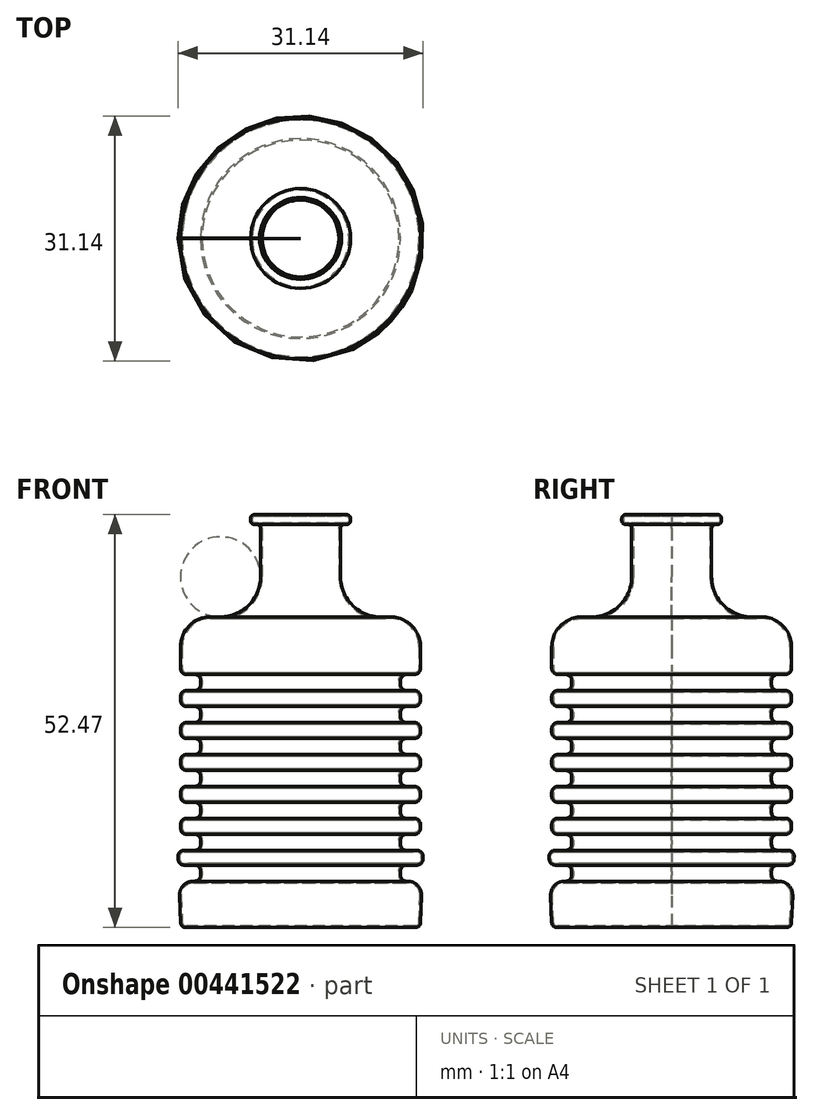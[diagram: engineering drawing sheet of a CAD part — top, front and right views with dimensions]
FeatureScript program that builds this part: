
annotation { "Feature Type Name" : "Feature", "Feature Type Description" : "" }
export const myFeature = defineFeature(function(context is Context, id is Id, definition is map)
    precondition{}
    {
        {
            var Q0;
            Q0=qCreatedBy(makeId("Front.planeOp"),FACE);
            var sketch = newSketch(context, id + "F0", { "sketchPlane" : qUnion([Q0])});
            skLineSegment(sketch, "E0", {"start": v(-5.2, 50.53) * mm, "end": v(-5.84, 50.53) * mm});
            skLineSegment(sketch, "E1", {"start": v(-6.35, 50.02) * mm, "end": v(-6.35, 49.77) * mm});
            skLineSegment(sketch, "E2", {"start": v(-5.84, 49.26) * mm, "end": v(-5.59, 49.26) * mm});
            skLineSegment(sketch, "E3", {"start": v(-5.08, 48.75) * mm, "end": v(-5.08, 46.72) * mm});
            skLineSegment(sketch, "E4", {"start": v(-5.08, 36.56) * mm, "end": v(-5.08, 36.56) * mm});
            skLineSegment(sketch, "E5", {"start": v(-15.24, 36.56) * mm, "end": v(-15.24, 36.56) * mm});
            skLineSegment(sketch, "E6", {"start": v(-14.6, -1.94) * mm, "end": v(-2.67, -1.94) * mm});
            skLineSegment(sketch, "E7", {"start": v(-15.24, 32.35) * mm, "end": v(-15.24, 30.97) * mm});
            skLineSegment(sketch, "E8", {"start": v(-14.48, 30.21) * mm, "end": v(-13.46, 30.21) * mm});
            skLineSegment(sketch, "E9", {"start": v(-12.7, 29.45) * mm, "end": v(-12.7, 28.94) * mm});
            skLineSegment(sketch, "E10", {"start": v(-13.46, 28.18) * mm, "end": v(-14.48, 28.18) * mm});
            skLineSegment(sketch, "E11", {"start": v(-15.24, 27.42) * mm, "end": v(-15.24, 26.9) * mm});
            skLineSegment(sketch, "E12", {"start": v(-14.48, 26.15) * mm, "end": v(-13.46, 26.15) * mm});
            skLineSegment(sketch, "E13", {"start": v(-12.7, 25.39) * mm, "end": v(-12.7, 24.88) * mm});
            skLineSegment(sketch, "E14", {"start": v(-13.46, 24.12) * mm, "end": v(-14.48, 24.12) * mm});
            skLineSegment(sketch, "E15", {"start": v(-15.24, 23.35) * mm, "end": v(-15.24, 22.85) * mm});
            skLineSegment(sketch, "E16", {"start": v(-14.48, 22.08) * mm, "end": v(-13.46, 22.08) * mm});
            skLineSegment(sketch, "E17", {"start": v(-12.7, 21.32) * mm, "end": v(-12.7, 20.81) * mm});
            skLineSegment(sketch, "E18", {"start": v(-13.46, 20.05) * mm, "end": v(-14.48, 20.05) * mm});
            skLineSegment(sketch, "E19", {"start": v(-15.24, 19.29) * mm, "end": v(-15.24, 18.8) * mm});
            skLineSegment(sketch, "E20", {"start": v(-14.48, 18.03) * mm, "end": v(-13.46, 18.03) * mm});
            skLineSegment(sketch, "E21", {"start": v(-12.7, 17.27) * mm, "end": v(-12.7, 16.76) * mm});
            skLineSegment(sketch, "E22", {"start": v(-13.46, 16) * mm, "end": v(-14.48, 16) * mm});
            skLineSegment(sketch, "E23", {"start": v(-15.24, 15.24) * mm, "end": v(-15.24, 14.73) * mm});
            skLineSegment(sketch, "E24", {"start": v(-14.48, 13.97) * mm, "end": v(-13.46, 13.97) * mm});
            skLineSegment(sketch, "E25", {"start": v(-12.7, 13.2) * mm, "end": v(-12.7, 12.7) * mm});
            skLineSegment(sketch, "E26", {"start": v(-13.46, 11.94) * mm, "end": v(-14.48, 11.94) * mm});
            skLineSegment(sketch, "E27", {"start": v(-15.24, 11.18) * mm, "end": v(-15.24, 10.67) * mm});
            skLineSegment(sketch, "E28", {"start": v(-14.48, 9.9) * mm, "end": v(-13.46, 9.9) * mm});
            skLineSegment(sketch, "E29", {"start": v(-12.7, 9.14) * mm, "end": v(-12.7, 8.64) * mm});
            skLineSegment(sketch, "E30", {"start": v(-13.46, 7.87) * mm, "end": v(-14.81, 7.87) * mm});
            skLineSegment(sketch, "E31", {"start": v(-15.57, 7.08) * mm, "end": v(-15.56, 6.72) * mm});
            skLineSegment(sketch, "E32", {"start": v(-14.8, 6) * mm, "end": v(-13.46, 6) * mm});
            skLineSegment(sketch, "E33", {"start": v(-12.7, 5.23) * mm, "end": v(-12.7, 4.72) * mm});
            skLineSegment(sketch, "E34", {"start": v(-13.46, 3.96) * mm, "end": v(-13.6, 3.96) * mm});
            skLineSegment(sketch, "E35.trimOffspring", {"start": v(-15.37, 2.1) * mm, "end": v(-15.24, -1.33) * mm});
            skPoint(sketch, "E36.visualSharp", {"position": v(-6.35, 50.53) * mm});
            skArc(sketch, "E36.filletArc", {"start": v(-5.84, 50.53) * mm, "mid": v(-6.2, 50.38) * mm, "end": v(-6.35, 50.02) * mm});
            skPoint(sketch, "E37.visualSharp", {"position": v(-6.35, 49.26) * mm});
            skArc(sketch, "E37.filletArc", {"start": v(-6.35, 49.77) * mm, "mid": v(-6.2, 49.4) * mm, "end": v(-5.84, 49.26) * mm});
            skPoint(sketch, "E38.visualSharp", {"position": v(-5.08, 49.26) * mm});
            skArc(sketch, "E38.filletArc", {"start": v(-5.08, 48.75) * mm, "mid": v(-5.23, 49.11) * mm, "end": v(-5.59, 49.26) * mm});
            skPoint(sketch, "E39.visualSharp", {"position": v(-5.08, 36.56) * mm});
            skPoint(sketch, "E40.visualSharp", {"position": v(-15.24, 36.56) * mm});
            skPoint(sketch, "E41.visualSharp", {"position": v(-15.24, 30.21) * mm});
            skArc(sketch, "E41.filletArc", {"start": v(-15.24, 30.97) * mm, "mid": v(-15.02, 30.43) * mm, "end": v(-14.48, 30.21) * mm});
            skPoint(sketch, "E42.visualSharp", {"position": v(-12.7, 30.21) * mm});
            skArc(sketch, "E42.filletArc", {"start": v(-12.7, 29.45) * mm, "mid": v(-12.92, 29.99) * mm, "end": v(-13.46, 30.21) * mm});
            skPoint(sketch, "E43.visualSharp", {"position": v(-12.7, 28.18) * mm});
            skArc(sketch, "E43.filletArc", {"start": v(-13.46, 28.18) * mm, "mid": v(-12.92, 28.4) * mm, "end": v(-12.7, 28.94) * mm});
            skPoint(sketch, "E44.visualSharp", {"position": v(-15.24, 28.18) * mm});
            skArc(sketch, "E44.filletArc", {"start": v(-14.48, 28.18) * mm, "mid": v(-15.02, 27.96) * mm, "end": v(-15.24, 27.42) * mm});
            skPoint(sketch, "E45.visualSharp", {"position": v(-15.24, 26.15) * mm});
            skArc(sketch, "E45.filletArc", {"start": v(-15.24, 26.9) * mm, "mid": v(-15.02, 26.37) * mm, "end": v(-14.48, 26.15) * mm});
            skPoint(sketch, "E46.visualSharp", {"position": v(-12.7, 26.15) * mm});
            skArc(sketch, "E46.filletArc", {"start": v(-12.7, 25.39) * mm, "mid": v(-12.92, 25.92) * mm, "end": v(-13.46, 26.15) * mm});
            skPoint(sketch, "E47.visualSharp", {"position": v(-12.7, 24.12) * mm});
            skArc(sketch, "E47.filletArc", {"start": v(-13.46, 24.12) * mm, "mid": v(-12.92, 24.34) * mm, "end": v(-12.7, 24.88) * mm});
            skPoint(sketch, "E48.visualSharp", {"position": v(-15.24, 24.12) * mm});
            skArc(sketch, "E48.filletArc", {"start": v(-14.48, 24.12) * mm, "mid": v(-15.02, 23.9) * mm, "end": v(-15.24, 23.35) * mm});
            skPoint(sketch, "E49.visualSharp", {"position": v(-15.24, 22.08) * mm});
            skArc(sketch, "E49.filletArc", {"start": v(-15.24, 22.85) * mm, "mid": v(-15.02, 22.3) * mm, "end": v(-14.48, 22.08) * mm});
            skPoint(sketch, "E50.visualSharp", {"position": v(-12.7, 22.08) * mm});
            skArc(sketch, "E50.filletArc", {"start": v(-12.7, 21.32) * mm, "mid": v(-12.92, 21.86) * mm, "end": v(-13.46, 22.08) * mm});
            skPoint(sketch, "E51.visualSharp", {"position": v(-12.7, 20.05) * mm});
            skArc(sketch, "E51.filletArc", {"start": v(-13.46, 20.05) * mm, "mid": v(-12.92, 20.27) * mm, "end": v(-12.7, 20.81) * mm});
            skPoint(sketch, "E52.visualSharp", {"position": v(-15.24, 20.05) * mm});
            skArc(sketch, "E52.filletArc", {"start": v(-14.48, 20.05) * mm, "mid": v(-15.02, 19.83) * mm, "end": v(-15.24, 19.29) * mm});
            skPoint(sketch, "E53.visualSharp", {"position": v(-15.24, 18.03) * mm});
            skArc(sketch, "E53.filletArc", {"start": v(-15.24, 18.8) * mm, "mid": v(-15.02, 18.26) * mm, "end": v(-14.48, 18.03) * mm});
            skPoint(sketch, "E54.visualSharp", {"position": v(-12.7, 18.03) * mm});
            skArc(sketch, "E54.filletArc", {"start": v(-12.7, 17.27) * mm, "mid": v(-12.92, 17.81) * mm, "end": v(-13.46, 18.03) * mm});
            skPoint(sketch, "E55.visualSharp", {"position": v(-12.7, 16) * mm});
            skArc(sketch, "E55.filletArc", {"start": v(-13.46, 16) * mm, "mid": v(-12.92, 16.23) * mm, "end": v(-12.7, 16.76) * mm});
            skPoint(sketch, "E56.visualSharp", {"position": v(-15.24, 16) * mm});
            skArc(sketch, "E56.filletArc", {"start": v(-14.48, 16) * mm, "mid": v(-15.02, 15.78) * mm, "end": v(-15.24, 15.24) * mm});
            skPoint(sketch, "E57.visualSharp", {"position": v(-15.24, 13.97) * mm});
            skArc(sketch, "E57.filletArc", {"start": v(-15.24, 14.73) * mm, "mid": v(-15.02, 14.2) * mm, "end": v(-14.48, 13.97) * mm});
            skPoint(sketch, "E58.visualSharp", {"position": v(-12.7, 13.97) * mm});
            skArc(sketch, "E58.filletArc", {"start": v(-12.7, 13.2) * mm, "mid": v(-12.92, 13.75) * mm, "end": v(-13.46, 13.97) * mm});
            skPoint(sketch, "E59.visualSharp", {"position": v(-12.7, 11.94) * mm});
            skArc(sketch, "E59.filletArc", {"start": v(-13.46, 11.94) * mm, "mid": v(-12.92, 12.16) * mm, "end": v(-12.7, 12.7) * mm});
            skPoint(sketch, "E60.visualSharp", {"position": v(-15.24, 11.94) * mm});
            skArc(sketch, "E60.filletArc", {"start": v(-14.48, 11.94) * mm, "mid": v(-15.02, 11.72) * mm, "end": v(-15.24, 11.18) * mm});
            skPoint(sketch, "E61.visualSharp", {"position": v(-15.24, 9.9) * mm});
            skArc(sketch, "E61.filletArc", {"start": v(-15.24, 10.67) * mm, "mid": v(-15.02, 10.13) * mm, "end": v(-14.48, 9.9) * mm});
            skPoint(sketch, "E62.visualSharp", {"position": v(-12.7, 9.9) * mm});
            skArc(sketch, "E62.filletArc", {"start": v(-12.7, 9.14) * mm, "mid": v(-12.92, 9.68) * mm, "end": v(-13.46, 9.9) * mm});
            skPoint(sketch, "E63.visualSharp", {"position": v(-12.7, 7.87) * mm});
            skArc(sketch, "E63.filletArc", {"start": v(-13.46, 7.87) * mm, "mid": v(-12.92, 8.1) * mm, "end": v(-12.7, 8.64) * mm});
            skPoint(sketch, "E64.visualSharp", {"position": v(-15.6, 7.87) * mm});
            skArc(sketch, "E64.filletArc", {"start": v(-14.81, 7.87) * mm, "mid": v(-15.36, 7.64) * mm, "end": v(-15.57, 7.08) * mm});
            skPoint(sketch, "E65.visualSharp", {"position": v(-15.53, 6) * mm});
            skArc(sketch, "E65.filletArc", {"start": v(-15.56, 6.72) * mm, "mid": v(-15.33, 6.2) * mm, "end": v(-14.8, 6) * mm});
            skPoint(sketch, "E66.visualSharp", {"position": v(-12.7, 6) * mm});
            skArc(sketch, "E66.filletArc", {"start": v(-12.7, 5.23) * mm, "mid": v(-12.92, 5.77) * mm, "end": v(-13.46, 6) * mm});
            skPoint(sketch, "E67.visualSharp", {"position": v(-12.7, 3.96) * mm});
            skArc(sketch, "E67.filletArc", {"start": v(-13.46, 3.96) * mm, "mid": v(-12.92, 4.18) * mm, "end": v(-12.7, 4.72) * mm});
            skPoint(sketch, "E68.visualSharp", {"position": v(-15.45, 3.96) * mm});
            skArc(sketch, "E68.filletArc", {"start": v(-13.6, 3.96) * mm, "mid": v(-14.88, 3.41) * mm, "end": v(-15.37, 2.1) * mm});
            skLineSegment(sketch, "E69.0", {"start": v(-5.2, 50.33) * mm, "end": v(-5.84, 50.33) * mm});
            skArc(sketch, "E70.0", {"start": v(-5.84, 50.33) * mm, "mid": v(-6.06, 50.24) * mm, "end": v(-6.15, 50.02) * mm});
            skLineSegment(sketch, "E71.0", {"start": v(-6.15, 50.02) * mm, "end": v(-6.15, 49.77) * mm});
            skArc(sketch, "E72.0", {"start": v(-6.15, 49.77) * mm, "mid": v(-6.06, 49.55) * mm, "end": v(-5.84, 49.46) * mm});
            skLineSegment(sketch, "E73.0", {"start": v(-5.84, 49.46) * mm, "end": v(-5.59, 49.46) * mm});
            skArc(sketch, "E74.0", {"start": v(-4.88, 48.75) * mm, "mid": v(-5.09, 49.26) * mm, "end": v(-5.59, 49.46) * mm});
            skLineSegment(sketch, "E75.0", {"start": v(-4.88, 48.75) * mm, "end": v(-4.88, 46.72) * mm});
            skLineSegment(sketch, "E76.0", {"start": v(-15.04, 32.35) * mm, "end": v(-15.04, 30.97) * mm});
            skArc(sketch, "E77.0", {"start": v(-15.04, 30.97) * mm, "mid": v(-14.87, 30.58) * mm, "end": v(-14.48, 30.41) * mm});
            skLineSegment(sketch, "E78.0", {"start": v(-14.48, 30.41) * mm, "end": v(-13.46, 30.41) * mm});
            skArc(sketch, "E79.0", {"start": v(-12.5, 29.45) * mm, "mid": v(-12.78, 30.13) * mm, "end": v(-13.46, 30.41) * mm});
            skLineSegment(sketch, "E80.0", {"start": v(-12.5, 29.45) * mm, "end": v(-12.5, 28.94) * mm});
            skArc(sketch, "E81.0", {"start": v(-13.46, 27.98) * mm, "mid": v(-12.78, 28.26) * mm, "end": v(-12.5, 28.94) * mm});
            skLineSegment(sketch, "E82.0", {"start": v(-13.46, 27.98) * mm, "end": v(-14.48, 27.98) * mm});
            skArc(sketch, "E83.0", {"start": v(-14.48, 27.98) * mm, "mid": v(-14.87, 27.81) * mm, "end": v(-15.04, 27.42) * mm});
            skArc(sketch, "E84.0", {"start": v(-15.04, 26.9) * mm, "mid": v(-14.87, 26.51) * mm, "end": v(-14.48, 26.35) * mm});
            skLineSegment(sketch, "E85.0", {"start": v(-15.04, 27.42) * mm, "end": v(-15.04, 26.9) * mm});
            skLineSegment(sketch, "E86.0", {"start": v(-14.48, 26.35) * mm, "end": v(-13.46, 26.35) * mm});
            skArc(sketch, "E87.0", {"start": v(-12.5, 25.39) * mm, "mid": v(-12.78, 26.07) * mm, "end": v(-13.46, 26.35) * mm});
            skLineSegment(sketch, "E88.0", {"start": v(-12.5, 25.39) * mm, "end": v(-12.5, 24.88) * mm});
            skArc(sketch, "E89.0", {"start": v(-13.46, 23.91) * mm, "mid": v(-12.78, 24.2) * mm, "end": v(-12.5, 24.88) * mm});
            skLineSegment(sketch, "E90.0", {"start": v(-13.46, 23.91) * mm, "end": v(-14.48, 23.91) * mm});
            skLineSegment(sketch, "E91.0", {"start": v(-14.48, 22.29) * mm, "end": v(-13.46, 22.29) * mm});
            skArc(sketch, "E91.1", {"start": v(-15.04, 22.85) * mm, "mid": v(-14.87, 22.45) * mm, "end": v(-14.48, 22.29) * mm});
            skLineSegment(sketch, "E91.2", {"start": v(-15.04, 23.35) * mm, "end": v(-15.04, 22.85) * mm});
            skArc(sketch, "E91.3", {"start": v(-14.48, 23.91) * mm, "mid": v(-14.87, 23.75) * mm, "end": v(-15.04, 23.35) * mm});
            skArc(sketch, "E92.0", {"start": v(-14.48, 19.85) * mm, "mid": v(-14.87, 19.68) * mm, "end": v(-15.04, 19.29) * mm});
            skLineSegment(sketch, "E93.0", {"start": v(-13.46, 19.85) * mm, "end": v(-14.48, 19.85) * mm});
            skLineSegment(sketch, "E94.0", {"start": v(-15.04, 19.29) * mm, "end": v(-15.04, 18.78) * mm});
            skArc(sketch, "E95.0", {"start": v(-15.04, 18.8) * mm, "mid": v(-14.87, 18.4) * mm, "end": v(-14.48, 18.24) * mm});
            skLineSegment(sketch, "E96.0", {"start": v(-14.48, 18.24) * mm, "end": v(-13.46, 18.24) * mm});
            skArc(sketch, "E97.0", {"start": v(-12.5, 21.32) * mm, "mid": v(-12.78, 22) * mm, "end": v(-13.46, 22.29) * mm});
            skLineSegment(sketch, "E98.0", {"start": v(-12.5, 21.32) * mm, "end": v(-12.5, 20.81) * mm});
            skArc(sketch, "E99.0", {"start": v(-13.46, 19.85) * mm, "mid": v(-12.78, 20.13) * mm, "end": v(-12.5, 20.81) * mm});
            skLineSegment(sketch, "E100.0", {"start": v(-12.5, 16.76) * mm, "end": v(-12.5, 16.76) * mm});
            skArc(sketch, "E101.0", {"start": v(-14.48, 15.8) * mm, "mid": v(-14.87, 15.64) * mm, "end": v(-15.04, 15.24) * mm});
            skLineSegment(sketch, "E102.0", {"start": v(-13.46, 15.8) * mm, "end": v(-14.48, 15.8) * mm});
            skLineSegment(sketch, "E103.0", {"start": v(-15.04, 14.73) * mm, "end": v(-15.04, 14.73) * mm});
            skArc(sketch, "E104.0", {"start": v(-15.04, 14.73) * mm, "mid": v(-14.87, 14.34) * mm, "end": v(-14.48, 14.17) * mm});
            skLineSegment(sketch, "E105.0", {"start": v(-14.48, 14.17) * mm, "end": v(-13.46, 14.17) * mm});
            skArc(sketch, "E106.0", {"start": v(-12.5, 13.2) * mm, "mid": v(-12.78, 13.9) * mm, "end": v(-13.46, 14.17) * mm});
            skLineSegment(sketch, "E107.0", {"start": v(-12.5, 12.7) * mm, "end": v(-12.5, 12.7) * mm});
            skArc(sketch, "E108.0", {"start": v(-13.46, 11.74) * mm, "mid": v(-12.78, 12.02) * mm, "end": v(-12.5, 12.7) * mm});
            skLineSegment(sketch, "E109.0", {"start": v(-13.46, 11.74) * mm, "end": v(-14.48, 11.74) * mm});
            skArc(sketch, "E110.0", {"start": v(-14.48, 11.74) * mm, "mid": v(-14.87, 11.57) * mm, "end": v(-15.04, 11.18) * mm});
            skLineSegment(sketch, "E111.0", {"start": v(-15.04, 11.18) * mm, "end": v(-15.04, 10.67) * mm});
            skArc(sketch, "E112.0", {"start": v(-15.04, 10.67) * mm, "mid": v(-14.87, 10.27) * mm, "end": v(-14.48, 10.1) * mm});
            skLineSegment(sketch, "E113.0", {"start": v(-14.48, 10.1) * mm, "end": v(-13.46, 10.1) * mm});
            skArc(sketch, "E114.0", {"start": v(-12.5, 9.14) * mm, "mid": v(-12.78, 9.83) * mm, "end": v(-13.46, 10.1) * mm});
            skLineSegment(sketch, "E115.0", {"start": v(-12.5, 8.64) * mm, "end": v(-12.5, 8.64) * mm});
            skLineSegment(sketch, "E116.0", {"start": v(-13.46, 7.67) * mm, "end": v(-14.81, 7.67) * mm});
            skLineSegment(sketch, "E117.0", {"start": v(-14.8, 6.2) * mm, "end": v(-13.46, 6.2) * mm});
            skPoint(sketch, "E118.visualSharp", {"position": v(-15.02, -1.74) * mm});
            skPoint(sketch, "E119.visualSharp", {"position": v(-15.21, -1.94) * mm});
            skArc(sketch, "E119.filletArc", {"start": v(-15.24, -1.33) * mm, "mid": v(-15.04, -1.77) * mm, "end": v(-14.6, -1.94) * mm});
            skPoint(sketch, "E120.orphan", {"position": v(0, 49.68) * mm});
            skLineSegment(sketch, "E121", {"start": v(-5.2, 50.53) * mm, "end": v(-5.2, 50.33) * mm});
            skPoint(sketch, "E122.orphan", {"position": v(0, 50.53) * mm});
            skPoint(sketch, "E123.end.orphan", {"position": v(0, -1.94) * mm});
            skLineSegment(sketch, "E124", {"start": v(-5.08, 46.72) * mm, "end": v(-5.08, 42.61) * mm});
            skLineSegment(sketch, "E125", {"start": v(-10.16, 37.53) * mm, "end": v(-11.43, 37.53) * mm});
            skLineSegment(sketch, "E126", {"start": v(-15.24, 33.72) * mm, "end": v(-15.24, 32.35) * mm});
            skPoint(sketch, "E127.visualSharp", {"position": v(-15.24, 37.53) * mm});
            skArc(sketch, "E127.filletArc", {"start": v(-11.43, 37.53) * mm, "mid": v(-14.12, 36.42) * mm, "end": v(-15.24, 33.72) * mm});
            skPoint(sketch, "E128.visualSharp", {"position": v(-5.08, 37.53) * mm});
            skArc(sketch, "E128.filletArc", {"start": v(-10.16, 37.53) * mm, "mid": v(-6.57, 39.02) * mm, "end": v(-5.08, 42.61) * mm});
            skArc(sketch, "E129.0", {"start": v(-11.43, 37.33) * mm, "mid": v(-13.98, 36.27) * mm, "end": v(-15.04, 33.72) * mm});
            skLineSegment(sketch, "E130.0", {"start": v(-15.04, 33.72) * mm, "end": v(-15.04, 32.35) * mm});
            skLineSegment(sketch, "E131.0", {"start": v(-10.16, 37.33) * mm, "end": v(-11.43, 37.33) * mm});
            skArc(sketch, "E132.0", {"start": v(-10.16, 37.33) * mm, "mid": v(-6.42, 38.88) * mm, "end": v(-4.88, 42.61) * mm});
            skLineSegment(sketch, "E133.0", {"start": v(-4.88, 46.72) * mm, "end": v(-4.88, 42.61) * mm});
            skLineSegment(sketch, "E134", {"start": v(0, 55.88) * mm, "end": v(0, -12.34) * mm});
            skArc(sketch, "E135.0", {"start": v(-14.81, 7.67) * mm, "mid": v(-15.22, 7.5) * mm, "end": v(-15.37, 7.1) * mm});
            skLineSegment(sketch, "E136.0", {"start": v(-15.37, 7.1) * mm, "end": v(-15.36, 6.73) * mm});
            skArc(sketch, "E137.0", {"start": v(-15.36, 6.73) * mm, "mid": v(-15.19, 6.35) * mm, "end": v(-14.8, 6.2) * mm});
            skArc(sketch, "E138.0", {"start": v(-13.46, 15.8) * mm, "mid": v(-12.78, 16.08) * mm, "end": v(-12.5, 16.76) * mm});
            skLineSegment(sketch, "E139.0", {"start": v(-12.5, 17.27) * mm, "end": v(-12.5, 16.76) * mm});
            skArc(sketch, "E140.0", {"start": v(-12.5, 17.27) * mm, "mid": v(-12.78, 17.96) * mm, "end": v(-13.46, 18.24) * mm});
            skLineSegment(sketch, "E141.0", {"start": v(-12.5, 13.2) * mm, "end": v(-12.5, 12.7) * mm});
            skLineSegment(sketch, "E142.0", {"start": v(-12.5, 9.14) * mm, "end": v(-12.5, 8.64) * mm});
            skArc(sketch, "E143.0", {"start": v(-13.46, 7.67) * mm, "mid": v(-12.78, 7.95) * mm, "end": v(-12.5, 8.64) * mm});
            skLineSegment(sketch, "E144.0", {"start": v(-14.6, -1.74) * mm, "end": v(-2.67, -1.74) * mm});
            skLineSegment(sketch, "E145.0", {"start": v(-15.17, 2.12) * mm, "end": v(-15.03, -1.32) * mm});
            skArc(sketch, "E146.0", {"start": v(-15.03, -1.32) * mm, "mid": v(-14.9, -1.62) * mm, "end": v(-14.6, -1.74) * mm});
            skArc(sketch, "E147.0", {"start": v(-13.6, 3.76) * mm, "mid": v(-14.73, 3.27) * mm, "end": v(-15.17, 2.12) * mm});
            skLineSegment(sketch, "E148.0", {"start": v(-13.46, 3.76) * mm, "end": v(-13.6, 3.76) * mm});
            skArc(sketch, "E149.0", {"start": v(-13.46, 3.76) * mm, "mid": v(-12.78, 4.04) * mm, "end": v(-12.5, 4.72) * mm});
            skLineSegment(sketch, "E150.0", {"start": v(-12.5, 5.23) * mm, "end": v(-12.5, 4.72) * mm});
            skArc(sketch, "E151.0", {"start": v(-12.5, 5.23) * mm, "mid": v(-12.78, 5.91) * mm, "end": v(-13.46, 6.2) * mm});
            skLineSegment(sketch, "E152.0", {"start": v(-15.04, 15.24) * mm, "end": v(-15.04, 14.73) * mm});
            skLineSegment(sketch, "E153", {"start": v(-2.67, -1.74) * mm, "end": v(0, -1.74) * mm});
            skLineSegment(sketch, "E154", {"start": v(0, -1.74) * mm, "end": v(0, -1.94) * mm});
            skLineSegment(sketch, "E155", {"start": v(0, -1.94) * mm, "end": v(-2.67, -1.94) * mm});
            skSolve(sketch);
        }
        {
            var Q0;
            Q0=makeQuery(id+"F0.imprint","IMPRINT",FACE,{"disambiguationData":[TD([[makeQuery(id+"F0.imprint","IMPRINT",EDGE,{"derivedFrom":sQuery(id+"F0.wireOp",EDGE,"E0")}),1.0]])]});
            var Q1;
            Q1=sQuery(id+"F0.wireOp",EDGE,"E134");
            revolve(context, id + "F1", {"entities" : qUnion([Q0]), "axis" : qUnion([Q1]), "revolveType" : RevolveType.ONE_DIRECTION, "oppositeDirection" : true, "angle" : 359.76 * degree});
        }
    });
